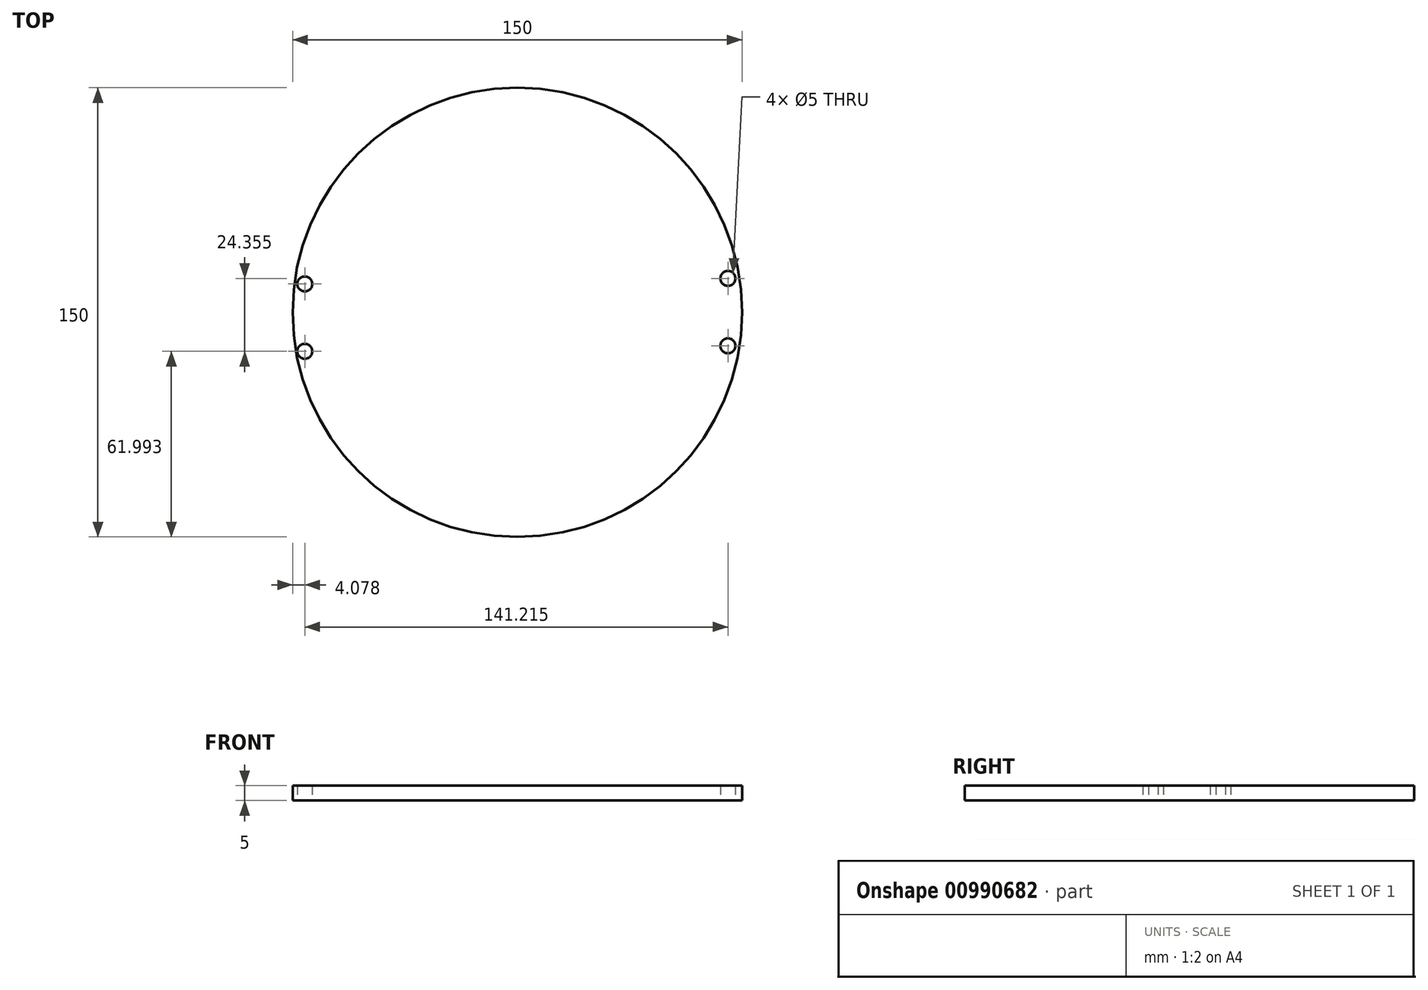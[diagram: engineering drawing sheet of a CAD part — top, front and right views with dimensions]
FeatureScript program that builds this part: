
annotation { "Feature Type Name" : "Feature", "Feature Type Description" : "" }
export const myFeature = defineFeature(function(context is Context, id is Id, definition is map)
    precondition{}
    {
        {
            var Q0;
            Q0=qCreatedBy(makeId("Top.planeOp"),FACE);
            var sketch = newSketch(context, id + "F0", { "sketchPlane" : qUnion([Q0])});
            skCircle(sketch, "E0", {"center": v(0, 0) * mm, "radius": 75 * mm});
            skSolve(sketch);
        }
        {
            var Q0;
            Q0=makeQuery(id+"F0.imprint","IMPRINT",FACE,{"disambiguationData":[TD([[makeQuery(id+"F0.imprint","IMPRINT",EDGE,{"derivedFrom":sQuery(id+"F0.wireOp",EDGE,"E0")}),1.0]])]});
            extrude(context, id + "F1", {"entities" : qUnion([Q0]), "depth" : 5 * mm, "offsetDistance" : 25 * mm});
        }
        {
            var Q0;
            Q0=qCreatedBy(makeId("Top.planeOp"),FACE);
            var sketch = newSketch(context, id + "F2", { "sketchPlane" : qUnion([Q0])});
            skLineSegment(sketch, "E1", {"start": v(70.3, 11.35) * mm, "end": v(70.3, -11.15) * mm});
            skSolve(sketch);
        }
        {
            var Q0;
            Q0=makeQuery(id+"F1.opExtrude","SWEPT_BODY",BODY,{"disambiguationData":[OSD([sQuery(id+"F0.wireOp",EDGE,"E0")])]});
            var Q1;
            Q1=qCreatedBy(makeId("Right.planeOp"),FACE);
            mirror(context, id + "F3", {"operationType" : NewBodyOperationType.ADD, "entities" : qUnion([Q0]), "mirrorPlane" : qUnion([Q1])});
        }
        {
            var Q0;
            Q0=qCreatedBy(makeId("Top.planeOp"),FACE);
            var sketch = newSketch(context, id + "F4", { "sketchPlane" : qUnion([Q0])});
            skLineSegment(sketch, "E2", {"start": v(-70.92, 9.5) * mm, "end": v(-70.92, -13) * mm});
            skSolve(sketch);
        }
        {
            var Q0;
            Q0=sQuery(id+"F4.wireOp",VERTEX,"E2.start");
            var Q1;
            Q1=sQuery(id+"F4.wireOp",VERTEX,"E2.end");
            var Q2;
            Q2=sQuery(id+"F2.wireOp",VERTEX,"E1.start");
            var Q3;
            Q3=sQuery(id+"F2.wireOp",VERTEX,"E1.end");
            var Q4;
            Q4=makeQuery(id+"F1.opExtrude","SWEPT_BODY",BODY,{"disambiguationData":[OSD([sQuery(id+"F0.wireOp",EDGE,"E0")])]});
            hole(context, id + "F5", {"style" : HoleStyle.SIMPLE, "endStyle" : HoleEndStyle.THROUGH, "oppositeDirection" : true, "holeDiameter" : 5 * mm, "majorDiameter" : 5 * mm, "isTappedThrough" : true, "tappedDepth" : 12 * mm, "tapClearance" : 3, "locations" : qUnion([Q0, Q1, Q2, Q3]), "scope" : qUnion([Q4])});
        }
    });
